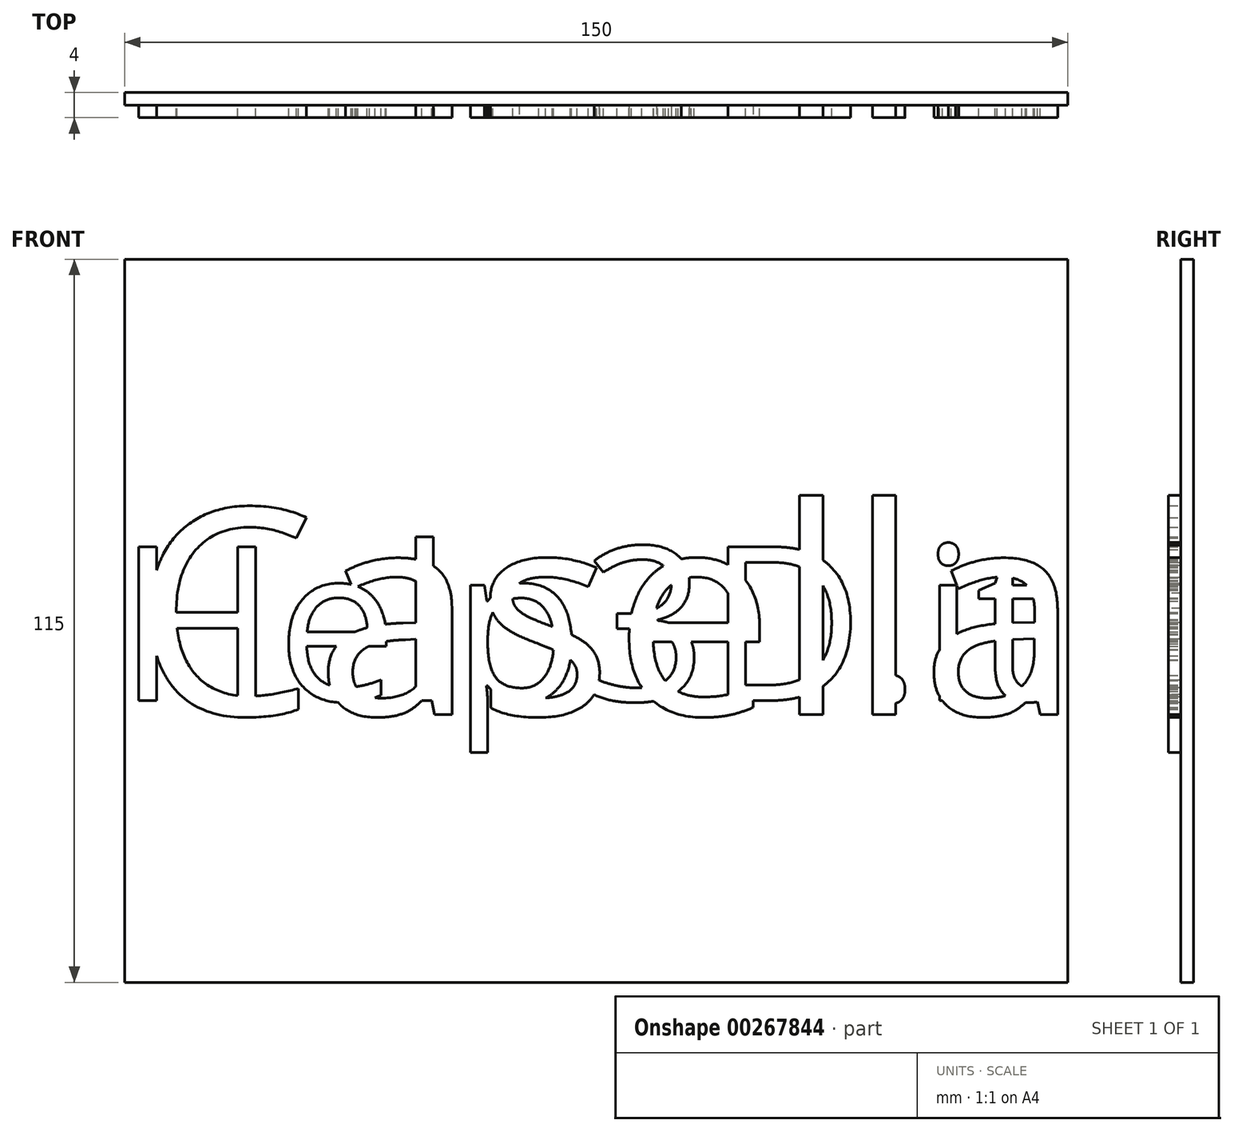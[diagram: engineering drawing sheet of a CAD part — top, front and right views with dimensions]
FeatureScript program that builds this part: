
annotation { "Feature Type Name" : "Feature", "Feature Type Description" : "" }
export const myFeature = defineFeature(function(context is Context, id is Id, definition is map)
    precondition{}
    {
        {
            var Q0;
            Q0=qCreatedBy(makeId("Front.planeOp"),FACE);
            var sketch = newSketch(context, id + "F0", { "sketchPlane" : qUnion([Q0])});
            skLineSegment(sketch, "E0.bottom", {"start": v(75, -57.5) * mm, "end": v(-75, -57.5) * mm});
            skLineSegment(sketch, "E0.top", {"start": v(75, 57.5) * mm, "end": v(-75, 57.5) * mm});
            skLineSegment(sketch, "E0.left", {"start": v(75, -57.5) * mm, "end": v(75, 57.5) * mm});
            skLineSegment(sketch, "E0.right", {"start": v(-75, -57.5) * mm, "end": v(-75, 57.5) * mm});
            skPoint(sketch, "E0.middle", {"position": v(0, 0) * mm});
            skSolve(sketch);
        }
        {
            var Q0;
            Q0=makeQuery(id+"F0.imprint","IMPRINT",FACE,{"disambiguationData":[TD([[makeQuery(id+"F0.imprint","IMPRINT",EDGE,{"derivedFrom":sQuery(id+"F0.wireOp",EDGE,"E0.bottom")}),-1.0]])]});
            extrude(context, id + "F1", {"entities" : qUnion([Q0]), "depth" : 2 * mm});
        }
        {
            var Q0;
            Q0=makeQuery(id+"F1.opExtrude","CAP_FACE",FACE,{"disambiguationData":[OSD([sQuery(id+"F0.wireOp",EDGE,"E0.bottom"),sQuery(id+"F0.wireOp",EDGE,"E0.top"),sQuery(id+"F0.wireOp",EDGE,"E0.left"),sQuery(id+"F0.wireOp",EDGE,"E0.right")])],"isStart":false});
            var sketch = newSketch(context, id + "F2", { "sketchPlane" : qUnion([Q0])});
            skText(sketch, "E1", { "text": "Help3D.it", "fontName": "OpenSans-Regular.ttf"});
            const initialGuessF2  = {"E1": [-0.0761, -0.01269, 1, 0, 0.02465]};
            skSetInitialGuess(sketch, initialGuessF2);
            skSolve(sketch);
        }
        {
            var Q0;
            Q0 = qSketchRegion(id + "F2", true);
            extrude(context, id + "F3", {"entities" : qUnion([Q0]), "operationType" : NewBodyOperationType.ADD, "depth" : 2 * mm});
        }
        {
            var Q0;
            Q0 = qSketchRegion(id + "F0", true);
            extrude(context, id + "F4", {"entities" : qUnion([Q0]), "depth" : 2 * mm});
        }
        {
            var Q0;
            Q0=makeQuery(id+"F4.opExtrude","CAP_FACE",FACE,{"disambiguationData":[OSD([sQuery(id+"F0.wireOp",EDGE,"E0.bottom"),sQuery(id+"F0.wireOp",EDGE,"E0.top"),sQuery(id+"F0.wireOp",EDGE,"E0.left"),sQuery(id+"F0.wireOp",EDGE,"E0.right")])],"isStart":false});
            var sketch = newSketch(context, id + "F5", { "sketchPlane" : qUnion([Q0])});
            skText(sketch, "E2", { "text": "Casella", "fontName": "OpenSans-Regular.ttf"});
            const initialGuessF5  = {"E2": [-0.07366, -0.01493, 1, 0, 0.03302]};
            skSetInitialGuess(sketch, initialGuessF5);
            skSolve(sketch);
        }
        {
            var Q0;
            Q0 = qSketchRegion(id + "F5", true);
            extrude(context, id + "F6", {"entities" : qUnion([Q0]), "operationType" : NewBodyOperationType.ADD, "depth" : 2 * mm});
        }
    });
